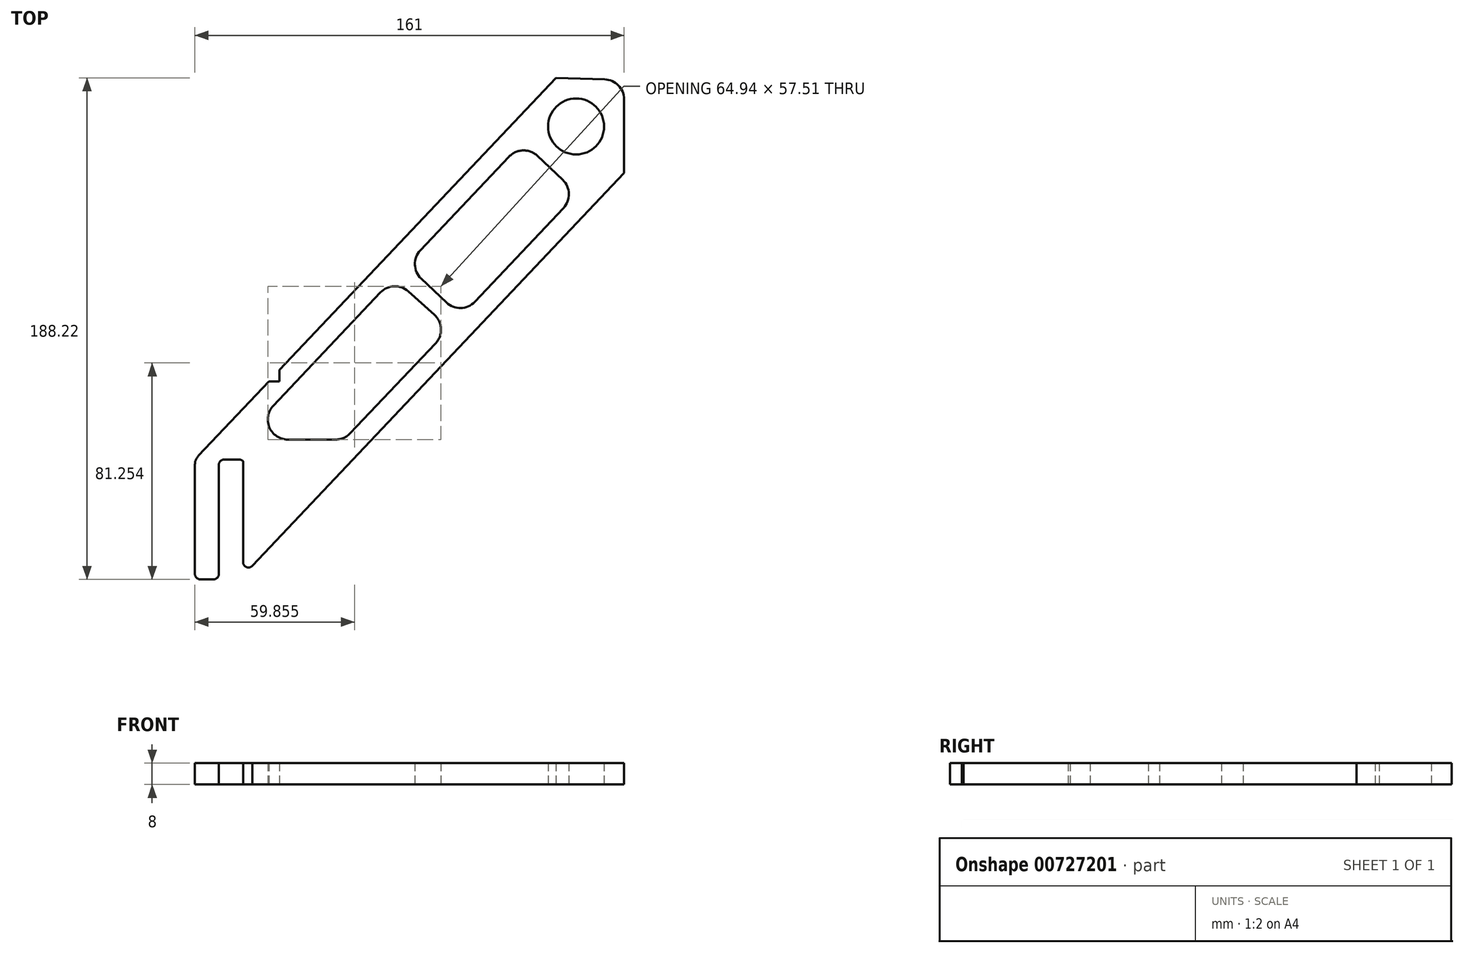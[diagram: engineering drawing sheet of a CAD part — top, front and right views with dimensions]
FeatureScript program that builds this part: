
annotation { "Feature Type Name" : "Feature", "Feature Type Description" : "" }
export const myFeature = defineFeature(function(context is Context, id is Id, definition is map)
    precondition{}
    {
        {
            var Q0;
            Q0=qCreatedBy(makeId("Top.planeOp"),FACE);
            var sketch = newSketch(context, id + "F0", { "sketchPlane" : qUnion([Q0]), "disableImprinting" : false});
            skLineSegment(sketch, "E0", {"start": v(0, 0) * mm, "end": v(0, 125) * mm, "construction": true});
            skLineSegment(sketch, "E1", {"start": v(0, 125) * mm, "end": v(125, 125) * mm, "construction": true});
            skCircle(sketch, "E2", {"center": v(125, 125) * mm, "radius": 10.5 * mm});
            skLineSegment(sketch, "E3", {"start": v(-1.43, 0) * mm, "end": v(-7.01, 0) * mm});
            skLineSegment(sketch, "E4", {"start": v(-11, -45) * mm, "end": v(-16, -45) * mm});
            skLineSegment(sketch, "E5", {"start": v(125, 125) * mm, "end": v(112.27, 112.27) * mm, "construction": true});
            skLineSegment(sketch, "E6", {"start": v(143, 135.2) * mm, "end": v(143, 125) * mm});
            skLineSegment(sketch, "E7", {"start": v(125, 125) * mm, "end": v(185, 125) * mm, "construction": true});
            skLineSegment(sketch, "E8", {"start": v(143, 125) * mm, "end": v(143, 107.5) * mm});
            skLineSegment(sketch, "E9", {"start": v(117.47, 143.22) * mm, "end": v(104.78, 129.8) * mm});
            skLineSegment(sketch, "E10", {"start": v(135.71, 142.7) * mm, "end": v(117.47, 143.22) * mm});
            skLineSegment(sketch, "E11", {"start": v(143, 107.5) * mm, "end": v(131.43, 95.26) * mm});
            skLineSegment(sketch, "E12", {"start": v(-18, 0) * mm, "end": v(41.31, 0) * mm, "construction": true});
            skPoint(sketch, "E13.visualSharp", {"position": v(143, 142.5) * mm});
            skArc(sketch, "E13.filletArc", {"start": v(143, 135.2) * mm, "mid": v(140.88, 140.44) * mm, "end": v(135.71, 142.7) * mm});
            skPoint(sketch, "E14.visualSharp", {"position": v(-9, 0) * mm});
            skArc(sketch, "E14.filletArc", {"start": v(-7.01, 0) * mm, "mid": v(-8.43, -0.59) * mm, "end": v(-9.01, -2) * mm});
            skPoint(sketch, "E15.visualSharp", {"position": v(0, 0) * mm});
            skArc(sketch, "E15.filletArc", {"start": v(0.09, -0.7) * mm, "mid": v(-0.6, -0.18) * mm, "end": v(-1.43, 0) * mm});
            skPoint(sketch, "E16.visualSharp", {"position": v(0, -45) * mm});
            skArc(sketch, "E16.filletArc", {"start": v(0.09, -38.56) * mm, "mid": v(1.36, -40.42) * mm, "end": v(3.56, -39.91) * mm});
            skLineSegment(sketch, "E17", {"start": v(104.78, 129.8) * mm, "end": v(13.75, 33.56) * mm});
            skLineSegment(sketch, "E18", {"start": v(41.31, 0) * mm, "end": v(41.31, 0) * mm});
            skLineSegment(sketch, "E19.0", {"start": v(16.84, 7.5) * mm, "end": v(34.85, 7.5) * mm});
            skLineSegment(sketch, "E20", {"start": v(131.43, 95.26) * mm, "end": v(131.43, 95.26) * mm});
            skLineSegment(sketch, "E21", {"start": v(131.43, 95.26) * mm, "end": v(3.56, -39.91) * mm});
            skLineSegment(sketch, "E22.0", {"start": v(120.26, 94.37) * mm, "end": v(86.99, 59.2) * mm});
            skLineSegment(sketch, "E23", {"start": v(38.08, 7.5) * mm, "end": v(38.08, 7.5) * mm});
            skLineSegment(sketch, "E24", {"start": v(110.47, 113.97) * mm, "end": v(119.97, 104.97) * mm});
            skLineSegment(sketch, "E25", {"start": v(99.86, 113.68) * mm, "end": v(66.58, 78.5) * mm});
            skPoint(sketch, "E26.visualSharp", {"position": v(125.4, 99.81) * mm});
            skArc(sketch, "E26.filletArc", {"start": v(120.26, 94.37) * mm, "mid": v(122.3, 99.73) * mm, "end": v(119.97, 104.97) * mm});
            skPoint(sketch, "E27.visualSharp", {"position": v(105.02, 119.14) * mm});
            skArc(sketch, "E27.filletArc", {"start": v(110.47, 113.97) * mm, "mid": v(105.1, 116.03) * mm, "end": v(99.86, 113.68) * mm});
            skPoint(sketch, "E28.visualSharp", {"position": v(-0.58, 7.5) * mm});
            skArc(sketch, "E28.filletArc", {"start": v(11.39, 20.15) * mm, "mid": v(9.95, 12.03) * mm, "end": v(16.84, 7.5) * mm});
            skPoint(sketch, "E29.visualSharp", {"position": v(38.08, 7.5) * mm});
            skArc(sketch, "E29.filletArc", {"start": v(34.85, 7.5) * mm, "mid": v(37.82, 8.11) * mm, "end": v(40.3, 9.85) * mm});
            skLineSegment(sketch, "E30", {"start": v(112.27, 112.27) * mm, "end": v(7.5, 7.5) * mm, "construction": true});
            skLineSegment(sketch, "E31", {"start": v(7.5, 7.5) * mm, "end": v(0, 0) * mm, "construction": true});
            skPoint(sketch, "E32.orphan", {"position": v(59.88, 59.88) * mm});
            skLineSegment(sketch, "E33.0.left", {"start": v(71.85, 54.3) * mm, "end": v(62.07, 63.09) * mm});
            skLineSegment(sketch, "E33.0.right", {"start": v(76.39, 58.9) * mm, "end": v(66.88, 67.9) * mm});
            skLineSegment(sketch, "E34", {"start": v(51.6, 62.67) * mm, "end": v(11.39, 20.15) * mm});
            skLineSegment(sketch, "E35", {"start": v(72.27, 43.56) * mm, "end": v(40.3, 9.85) * mm});
            skPoint(sketch, "E36.visualSharp", {"position": v(61.43, 73.05) * mm});
            skArc(sketch, "E36.filletArc", {"start": v(66.58, 78.5) * mm, "mid": v(64.53, 73.14) * mm, "end": v(66.88, 67.9) * mm});
            skPoint(sketch, "E37.visualSharp", {"position": v(81.83, 53.75) * mm});
            skArc(sketch, "E37.filletArc", {"start": v(76.39, 58.9) * mm, "mid": v(81.75, 56.86) * mm, "end": v(86.99, 59.2) * mm});
            skPoint(sketch, "E38.visualSharp", {"position": v(77.57, 49.14) * mm});
            skArc(sketch, "E38.filletArc", {"start": v(72.27, 43.56) * mm, "mid": v(74.32, 49.02) * mm, "end": v(71.85, 54.3) * mm});
            skPoint(sketch, "E39.visualSharp", {"position": v(56.63, 67.98) * mm});
            skArc(sketch, "E39.filletArc", {"start": v(62.07, 63.09) * mm, "mid": v(56.75, 65) * mm, "end": v(51.6, 62.67) * mm});
            skLineSegment(sketch, "E40", {"start": v(-18, -43) * mm, "end": v(-18, -2) * mm});
            skLineSegment(sketch, "E41", {"start": v(-16.63, 1.45) * mm, "end": v(9.75, 29.34) * mm});
            skLineSegment(sketch, "E42", {"start": v(9.75, 29.34) * mm, "end": v(13.75, 29.34) * mm});
            skLineSegment(sketch, "E43", {"start": v(13.75, 29.34) * mm, "end": v(13.75, 33.56) * mm});
            skPoint(sketch, "E44.0.visualSharp", {"position": v(-18, -45) * mm});
            skArc(sketch, "E44.0.filletArc", {"start": v(-18, -43) * mm, "mid": v(-17.41, -44.41) * mm, "end": v(-16, -45) * mm});
            skArc(sketch, "E45.0.filletArc", {"start": v(-11, -45) * mm, "mid": v(-9.59, -44.41) * mm, "end": v(-9, -43) * mm});
            skLineSegment(sketch, "E46", {"start": v(0.09, -38.56) * mm, "end": v(0.09, -0.7) * mm});
            skLineSegment(sketch, "E47", {"start": v(-9, -43) * mm, "end": v(-9.01, -2) * mm});
            skPoint(sketch, "E48.0.visualSharp", {"position": v(-18, 0) * mm});
            skArc(sketch, "E48.0.filletArc", {"start": v(-16.63, 1.45) * mm, "mid": v(-17.65, -0.14) * mm, "end": v(-18, -2) * mm});
            skSolve(sketch);
        }
        {
            var Q0;
            Q0=makeQuery(id+"F0.imprint","IMPRINT",FACE,{"disambiguationData":[TD([[makeQuery(id+"F0.imprint","IMPRINT",EDGE,{"derivedFrom":sQuery(id+"F0.wireOp",EDGE,"E2")}),-1.0]])]});
            extrude(context, id + "F1", {"entities" : qUnion([Q0]), "depth" : 8 * mm, "offsetDistance" : 25 * mm});
        }
    });
